# Revit family: QF_ACFRI_AR320-P850.190709093044
name_source: partatom
category: Specialty Equipment
revit_build: Autodesk Revit 2016 (Build: 20150220_1215(x64)
units: mm (PartAtom-declared; Revit-internal decimal feet)

## family parameters
Always vertical = Yes
Cut with Voids When Loaded = No
OmniClass Number = 23.40.40.14
OmniClass Title = Food Service Equipment
Part Type = Normal
Room Calculation Point = No
Round Connector Dimension = Use Diameter
Shared = No
Work Plane-Based = No

## types (1)
- AR320-P850_400V/0Ph/50Hz
    Accessoires = No
    Consommation d'énergie minimale = 0 A
    Cost = 0 $
    Câble de connexion à l'appareil inclus = No
    Description = GROUPE À AIR À DISTANCE BASIC
    Fréquence = 50 Hz
    Hauteur hors tout = 2270 mm  [stored 7.44751 ft]
    Intensité nominale courant electrique = 11 A
    Longueur hors tout = 1310 mm  [stored 4.2979 ft]
    Manufacturer = ACFRI
    Model = AR320-P850
    Nombres de Pôles = 1
    Phase = 1
    Poids net à vide = 0.00 kg
    Profondeur hors tout = 1780 mm  [stored 5.8399 ft]
    Protection de l'Appareil = 0 A
    Puissance Apparente = 17422 VA
    Puissance électrique  = 17422 W
    Tension = 400 V
    URL = www.acfri.com

note: [stored X ft] marks values corroborated as IEEE doubles in the binary element streams (Revit-internal decimal feet)

## geometry (parser evidence)
native form markers: Sweep x5
no freeform markers — native parametric forms only
